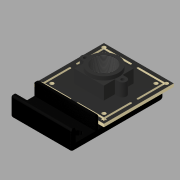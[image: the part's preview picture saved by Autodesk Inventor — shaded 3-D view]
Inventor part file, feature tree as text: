
AUTODESK INVENTOR PART (.ipt)
format: ipt  version: 2019 (Build 230136000, 136)  size: 387,072 bytes
history: native  units: mm
features: other x5, extrude x5, sketch x5, fillet x1
ambient origin geometry x8: Origin, YZ Plane, XZ Plane, XY Plane, X Axis, Y Axis, Z Axis, Center Point
bodies: Solid5 (feature_tree), Solid3 (feature_tree), Solid4 (feature_tree), Solid1 (feature_tree)
feature tree (16):
  other  "Spinel USB Camera 01.ipt"
  extrude  "Extrusion1"  Depth=10.0mm
  extrude  "Extrusion2"  Depth=1.5mm
  extrude  "Extrusion6"  Depth=1.5mm
  fillet  "Fillet2"  Radius=0.25mm
  extrude  "Extrusion7"  Depth=0.25mm
  extrude  "Extrusion8"  Depth=0.5mm
  other  "Solid1::Spinel USB Camera 01.ipt"
  other  "Solid2::Spinel USB Camera 01.ipt"
  other  "Solid3::Spinel USB Camera 01.ipt"
  other  "TaggingFeature2"
  sketch  "Sketch1"  dims[d1=10.0mm d12=1.5mm]
  sketch  "Sketch2"  dims[d13=0.25mm d14=1.5mm]
  sketch  "Sketch6"  dims[d15=0.25mm d16=1.5mm d17=0.25mm]
  sketch  "Sketch7"  dims[d18=1.5mm d19=0.25mm]
  sketch  "Sketch8"  dims[d20=2.0mm d21=0.0mm d22=2.5mm d23=135.0deg d24=0.5mm d25=0.5mm d26=4.25mm d27=4.25mm d34=3.5mm d35=0.0mm d47=20.0mm d48=11.0mm d49=2.0mm d50=2.0mm d51=7.0mm d52=0.0mm d53=1.0mm d54=3.35mm d55=3.35mm d56=25.4mm d57=33.3mm d58=3.95mm d59=7.0mm d60=0.0mm d61=6.5mm d62=6.5mm d63=1.0mm d64=0.0mm]
